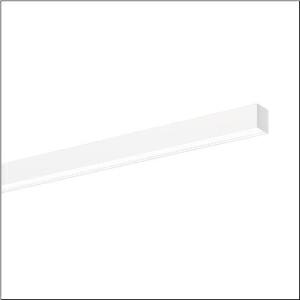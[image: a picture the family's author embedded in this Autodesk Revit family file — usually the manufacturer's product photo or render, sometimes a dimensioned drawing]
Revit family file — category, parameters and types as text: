
# Revit family: silica_21_51mx20db42wb
name_source: partatom
category: Lighting Fixtures
units: mm (PartAtom-declared; Revit-internal decimal feet)

## family parameters
Cut with Voids When Loaded = No
Host = Face
Light Source = No
Part Type = Normal
Room Calculation Point = No
Round Connector Dimension = Use Diameter
Shared = No

## types (1)
- --- (1 x LED, 3000 lm, 19 W, 4000K)
    Apparent Load = 19 VA
    CIE Flux Codes = 48 79 96 100 100
    Color Rendering = 80
    Color Temperature = 4000K
    Default Elevation = 1800 mm
    Description = Silica 21, office luminaire, primary optical cover: cover, of PMMA, opal, light emission: direct distribution, primary light characteristic: symmetric, installation type: surface-mounted, LED, rated luminous flux: 3.000lm, luminous efficacy: 158lm/W, light colour: 840, colour temperature: 4000K, control gear: DALI 2, with terminal, 3+2-pole, max. 2.5mm², mains connection: 220..240V, AC, 50/60Hz, rated input power: 19W, luminaire housing, of aluminium, traffic white (RAL 9016), length: 1.504mm, width: 53mm, height: 53mm, protection rating (complete): IP20, insulation class (complete): insulation class I (protective earthing), certification: CE, permissible operating ambient temperature: 0..+35°C, standard: EN 50419, packaging unit: 1 piece
    Height = 53 mm
    Lamp = 1 x LED
    Lamp Light Flux = 3000 lm
    Lamp Power = 19 W
    Lamp count = 1
    Length = 1504 mm
    Luminous efficacy = 158 lm/W
    Manufacturer = Siteco
    ModVariant = No
    Model = 51MX20DB42WB
    Mounting Place = Ceiling
    Mounting Type = Surface mounted
    Number of Poles = 1
    OnlyDefault = Yes
    Power Factor = 1
    Product Name = Silica 21
    Product group = office luminaire | ceiling mounted
    ProductGroupID = 301
    Protection Class = Protection class I
    Protection Degree = IP 20
    RLX_Detail_Level = 1
    RLX_Emergency_Light_Flux = 0 lm
    RLX_Emergency_Type = 0
    RLX_Emergency_Type_DB = No
    RlxData = <blob elided: 23753 chars, md5=ca6c290e>
    Socket = socket
    Standby Power = 0 W
    System Light Flux = 3000 lm
    System Power = 19 W
    Type Comments = factory setting: luminous flux: 100 % | dim-lin: 254 | 218 mA
    Type Image = l_1335877.jpg
    URL = http://relux.com
    VarID = @adj_119893
    Voltage = 0 V
    Weight = 0.00 kg
    Width = 53 mm

## geometry (parser evidence)
native form markers: Blend x4, Sweep x11
no freeform markers — native parametric forms only
